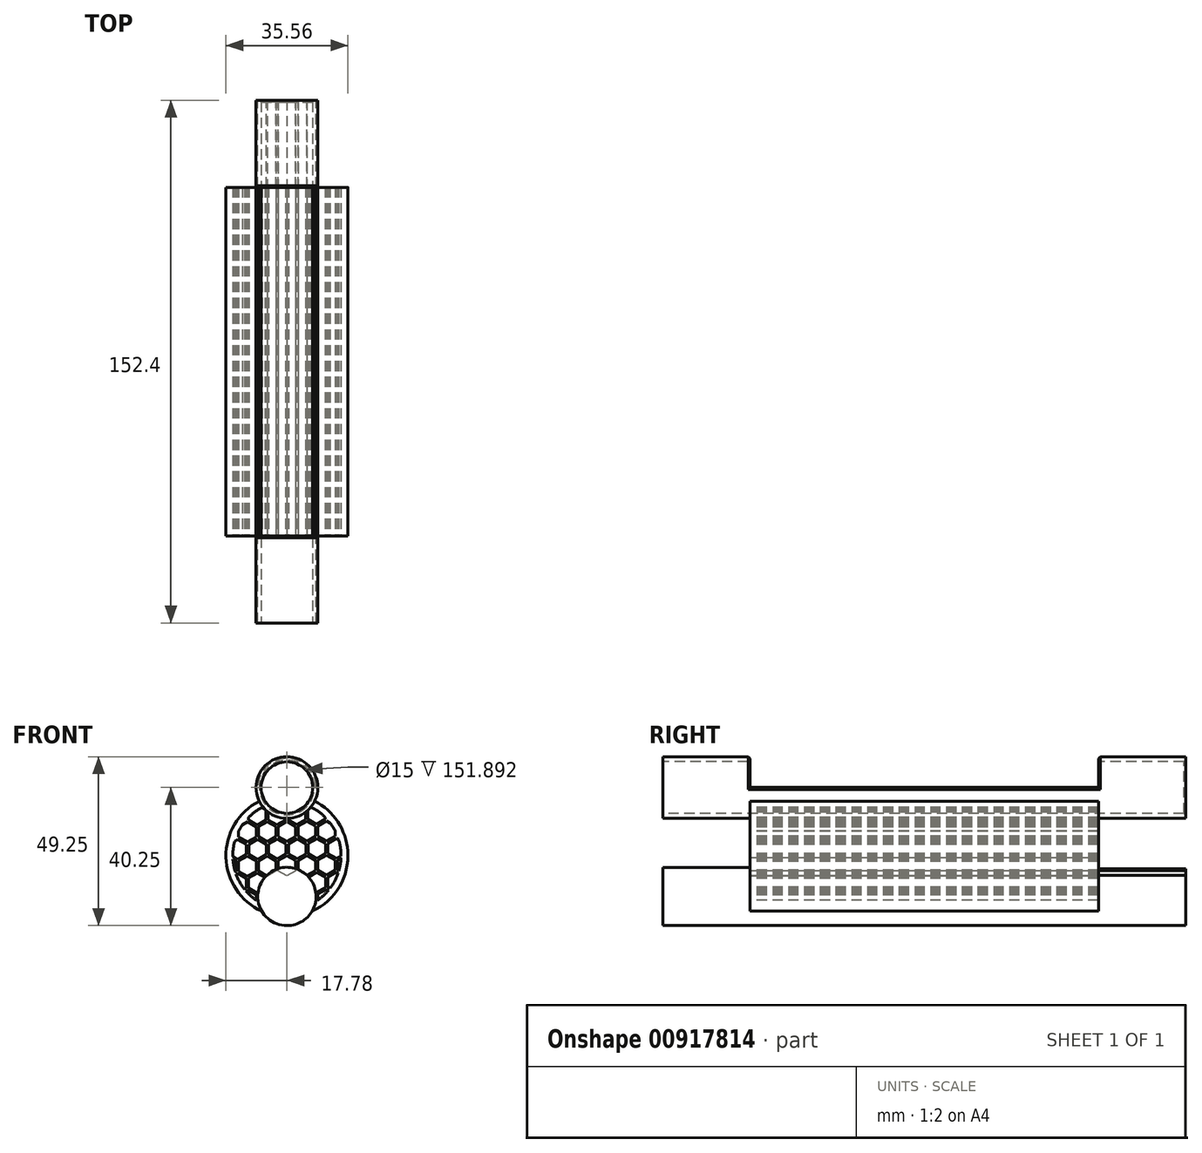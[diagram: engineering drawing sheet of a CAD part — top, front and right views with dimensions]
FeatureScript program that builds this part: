
annotation { "Feature Type Name" : "Feature", "Feature Type Description" : "" }
export const myFeature = defineFeature(function(context is Context, id is Id, definition is map)
    precondition{}
    {
        {
            var Q0;
            Q0=qCreatedBy(makeId("Front.planeOp"),FACE);
            var sketch = newSketch(context, id + "F0", { "sketchPlane" : qUnion([Q0])});
            skCircle(sketch, "E0", {"center": v(0, 0) * mm, "radius": 9 * mm});
            skCircle(sketch, "E1", {"center": v(0, -31.75) * mm, "radius": 8.5 * mm});
            skSolve(sketch);
        }
        {
            var Q0;
            Q0=qSketchRegion(id+"FUGsYxlSOq7sT89_0",true);
            var Q1;
            Q1=makeQuery(id+"F0.imprint","IMPRINT",FACE,{"disambiguationData":[TD([[makeQuery(id+"F0.imprint","IMPRINT",EDGE,{"derivedFrom":sQuery(id+"F0.wireOp",EDGE,"E0")}),1.0]])]});
            var Q2;
            Q2=makeQuery(id+"F0.imprint","IMPRINT",FACE,{"disambiguationData":[TD([[makeQuery(id+"F0.imprint","IMPRINT",EDGE,{"derivedFrom":sQuery(id+"F0.wireOp",EDGE,"E1")}),1.0]])]});
            extrude(context, id + "F1", {"entities" : qUnion([Q0, Q1, Q2]), "endBound" : BoundingType.SYMMETRIC, "depth" : 152.4 * mm, "offsetDistance" : 25.4 * mm});
        }
        {
            var Q0;
            Q0=makeQuery(id+"F1.opExtrude","CAP_FACE",FACE,{"disambiguationData":[OSD([sQuery(id+"F0.wireOp",EDGE,"E0")])],"isStart":false});
            var sketch = newSketch(context, id + "F2", { "sketchPlane" : qUnion([Q0])});
            skCircle(sketch, "E2", {"center": v(0, 0) * mm, "radius": 7.5 * mm});
            skSolve(sketch);
        }
        {
            var Q0;
            Q0=qSketchRegion(id+"F2",true);
            extrude(context, id + "F3", {"entities" : qUnion([Q0]), "operationType" : NewBodyOperationType.REMOVE, "endBound" : BoundingType.THROUGH_ALL, "oppositeDirection" : true, "depth" : 25.4 * mm, "offsetDistance" : 25.4 * mm});
        }
        {
            var Q0;
            Q0=makeQuery(id+"F0.imprint","IMPRINT",FACE,{"disambiguationData":[TD([[makeQuery(id+"F0.imprint","IMPRINT",EDGE,{"derivedFrom":sQuery(id+"F0.wireOp",EDGE,"E0")}),1.0]])]});
            var sketch = newSketch(context, id + "F4", { "sketchPlane" : qUnion([Q0])});
            skLineSegment(sketch, "E3.bottom", {"start": v(-11.18, 12.2) * mm, "end": v(12.33, 12.2) * mm});
            skLineSegment(sketch, "E3.top", {"start": v(-11.18, 0) * mm, "end": v(12.33, 0) * mm});
            skLineSegment(sketch, "E3.left", {"start": v(-11.18, 12.2) * mm, "end": v(-11.18, 0) * mm});
            skLineSegment(sketch, "E3.right", {"start": v(12.33, 12.2) * mm, "end": v(12.33, 0) * mm});
            skSolve(sketch);
        }
        {
            var Q0;
            Q0=qSketchRegion(id+"F4",true);
            extrude(context, id + "F5", {"entities" : qUnion([Q0]), "operationType" : NewBodyOperationType.REMOVE, "endBound" : BoundingType.SYMMETRIC, "oppositeDirection" : true, "depth" : 101.6 * mm, "offsetDistance" : 25.4 * mm});
        }
        {
            var Q0;
            Q0=makeQuery(id+"F5.boolean.opBoolean","INTERSECT",EDGE,{"disambiguationData":[OD(0.0)],"derivedFrom":[makeQuery(id+"F1.opExtrude","SWEPT_FACE",FACE,{"disambiguationData":[OSD([sQuery(id+"F0.wireOp",EDGE,"E0")])]}),makeQuery(id+"F5.opExtrude","SWEPT_FACE",FACE,{"disambiguationData":[OSD([sQuery(id+"F4.wireOp",EDGE,"E3.top")])]})]});
            var Q1;
            Q1=makeQuery(id+"F5.boolean.opBoolean","INTERSECT",EDGE,{"disambiguationData":[OD(1.0)],"derivedFrom":[makeQuery(id+"F1.opExtrude","SWEPT_FACE",FACE,{"disambiguationData":[OSD([sQuery(id+"F0.wireOp",EDGE,"E0")])]}),makeQuery(id+"F5.opExtrude","SWEPT_FACE",FACE,{"disambiguationData":[OSD([sQuery(id+"F4.wireOp",EDGE,"E3.top")])]})]});
            var Q2;
            Q2=makeQuery(id+"F5.boolean.opBoolean","INTERSECT",EDGE,{"disambiguationData":[OD(1.0)],"derivedFrom":[makeQuery(id+"F3.boolean.opBoolean","COPY",FACE,{"derivedFrom":makeQuery(id+"F3.opExtrude","SWEPT_FACE",FACE,{"disambiguationData":[OSD([sQuery(id+"F2.wireOp",EDGE,"E2")])]})}),makeQuery(id+"F5.opExtrude","SWEPT_FACE",FACE,{"disambiguationData":[OSD([sQuery(id+"F4.wireOp",EDGE,"E3.top")])]})]});
            var Q3;
            Q3=makeQuery(id+"F5.boolean.opBoolean","INTERSECT",EDGE,{"disambiguationData":[OD(0.0)],"derivedFrom":[makeQuery(id+"F3.boolean.opBoolean","COPY",FACE,{"derivedFrom":makeQuery(id+"F3.opExtrude","SWEPT_FACE",FACE,{"disambiguationData":[OSD([sQuery(id+"F2.wireOp",EDGE,"E2")])]})}),makeQuery(id+"F5.opExtrude","SWEPT_FACE",FACE,{"disambiguationData":[OSD([sQuery(id+"F4.wireOp",EDGE,"E3.top")])]})]});
            var Q4;
            Q4=makeQuery(id+"F5.boolean.opBoolean","INTERSECT",EDGE,{"derivedFrom":[makeQuery(id+"F1.opExtrude","SWEPT_FACE",FACE,{"disambiguationData":[OSD([sQuery(id+"F0.wireOp",EDGE,"E0")])]}),makeQuery(id+"F5.opExtrude","CAP_FACE",FACE,{"disambiguationData":[OSD([sQuery(id+"F4.wireOp",EDGE,"E3.bottom"),sQuery(id+"F4.wireOp",EDGE,"E3.top"),sQuery(id+"F4.wireOp",EDGE,"E3.left"),sQuery(id+"F4.wireOp",EDGE,"E3.right")])],"isStart":true})]});
            var Q5;
            Q5=makeQuery(id+"F5.boolean.opBoolean","INTERSECT",EDGE,{"derivedFrom":[makeQuery(id+"F1.opExtrude","SWEPT_FACE",FACE,{"disambiguationData":[OSD([sQuery(id+"F0.wireOp",EDGE,"E0")])]}),makeQuery(id+"F5.opExtrude","CAP_FACE",FACE,{"disambiguationData":[OSD([sQuery(id+"F4.wireOp",EDGE,"E3.bottom"),sQuery(id+"F4.wireOp",EDGE,"E3.top"),sQuery(id+"F4.wireOp",EDGE,"E3.left"),sQuery(id+"F4.wireOp",EDGE,"E3.right")])],"isStart":false})]});
            var Q6;
            Q6=makeQuery(id+"F5.boolean.opBoolean","INTERSECT",EDGE,{"derivedFrom":[makeQuery(id+"F3.boolean.opBoolean","COPY",FACE,{"derivedFrom":makeQuery(id+"F3.opExtrude","SWEPT_FACE",FACE,{"disambiguationData":[OSD([sQuery(id+"F2.wireOp",EDGE,"E2")])]})}),makeQuery(id+"F5.opExtrude","CAP_FACE",FACE,{"disambiguationData":[OSD([sQuery(id+"F4.wireOp",EDGE,"E3.bottom"),sQuery(id+"F4.wireOp",EDGE,"E3.top"),sQuery(id+"F4.wireOp",EDGE,"E3.left"),sQuery(id+"F4.wireOp",EDGE,"E3.right")])],"isStart":false})]});
            var Q7;
            Q7=makeQuery(id+"F5.boolean.opBoolean","INTERSECT",EDGE,{"derivedFrom":[makeQuery(id+"F3.boolean.opBoolean","COPY",FACE,{"derivedFrom":makeQuery(id+"F3.opExtrude","SWEPT_FACE",FACE,{"disambiguationData":[OSD([sQuery(id+"F2.wireOp",EDGE,"E2")])]})}),makeQuery(id+"F5.opExtrude","CAP_FACE",FACE,{"disambiguationData":[OSD([sQuery(id+"F4.wireOp",EDGE,"E3.bottom"),sQuery(id+"F4.wireOp",EDGE,"E3.top"),sQuery(id+"F4.wireOp",EDGE,"E3.left"),sQuery(id+"F4.wireOp",EDGE,"E3.right")])],"isStart":true})]});
            var Q8;
            Q8=makeQuery(id+"F3.boolean.opBoolean","INTERSECT",EDGE,{"derivedFrom":[makeQuery(id+"F1.opExtrude","CAP_FACE",FACE,{"disambiguationData":[OSD([sQuery(id+"F0.wireOp",EDGE,"E0")])],"isStart":true}),makeQuery(id+"F3.opExtrude","SWEPT_FACE",FACE,{"disambiguationData":[OSD([sQuery(id+"F2.wireOp",EDGE,"E2")])]})]});
            var Q9;
            Q9=makeQuery(id+"F3.boolean.opBoolean","COPY",EDGE,{"derivedFrom":makeQuery(id+"F3.opExtrude","CAP_EDGE",EDGE,{"disambiguationData":[OSD([sQuery(id+"F2.wireOp",EDGE,"E2")])],"isStart":true})});
            chamfer(context, id + "F6", {"entities" : qUnion([Q0, Q1, Q2, Q3, Q4, Q5, Q6, Q7, Q8, Q9]), "width" : 0.5 * mm, "tangentPropagation" : true});
        }
        {
            var Q0;
            Q0=qCreatedBy(makeId("Front.planeOp"),FACE);
            var sketch = newSketch(context, id + "F7", { "sketchPlane" : qUnion([Q0])});
            skLineSegment(sketch, "E4.0", {"start": v(2, -31.75) * mm, "end": v(2, -8.64) * mm});
            skLineSegment(sketch, "E5.0", {"start": v(-2, -31.75) * mm, "end": v(-2, -8.64) * mm});
            skPoint(sketch, "E6.start.orphan", {"position": v(0, -31.75) * mm});
            skLineSegment(sketch, "E7", {"start": v(-2, -31.75) * mm, "end": v(2, -31.75) * mm});
            skLineSegment(sketch, "E8", {"start": v(2, -8.64) * mm, "end": v(-2, -8.64) * mm});
            skSolve(sketch);
        }
        {
            var Q0;
            Q0=qSketchRegion(id+"F7",true);
            extrude(context, id + "F8", {"entities" : qUnion([Q0]), "operationType" : NewBodyOperationType.ADD, "endBound" : BoundingType.SYMMETRIC, "oppositeDirection" : true, "depth" : 101.6 * mm, "offsetDistance" : 25.4 * mm});
        }
        {
            var Q0;
            Q0=qCreatedBy(makeId("Front.planeOp"),FACE);
            var sketch = newSketch(context, id + "F9", { "sketchPlane" : qUnion([Q0])});
            skCircle(sketch, "E9", {"center": v(0, -19.81) * mm, "radius": 17.78 * mm});
            skSolve(sketch);
        }
        {
            var Q0;
            Q0=qSketchRegion(id+"F9",true);
            extrude(context, id + "F10", {"entities" : qUnion([Q0]), "operationType" : NewBodyOperationType.ADD, "endBound" : BoundingType.SYMMETRIC, "depth" : 101.6 * mm, "offsetDistance" : 25.4 * mm});
        }
        {
            var Q0;
            Q0=makeQuery(id+"F0.imprint","IMPRINT",FACE,{"disambiguationData":[TD([[makeQuery(id+"F0.imprint","IMPRINT",EDGE,{"derivedFrom":sQuery(id+"F0.wireOp",EDGE,"E0")}),1.0]])]});
            var sketch = newSketch(context, id + "F11", { "sketchPlane" : qUnion([Q0])});
            skCircle(sketch, "E10", {"center": v(0, 0) * mm, "radius": 7.5 * mm});
            skSolve(sketch);
        }
        {
            var Q0;
            Q0=qSketchRegion(id+"F11",true);
            extrude(context, id + "F12", {"entities" : qUnion([Q0]), "operationType" : NewBodyOperationType.REMOVE, "endBound" : BoundingType.SYMMETRIC, "oppositeDirection" : true, "depth" : 152.4 * mm, "offsetDistance" : 25.4 * mm});
        }
        {
            var Q0;
            Q0=makeQuery(id+"F10.boolean.opBoolean","MERGE",FACE,{"derivedFrom":[makeQuery(id+"F8.opExtrude","CAP_FACE",FACE,{"disambiguationData":[OSD([sQuery(id+"F7.wireOp",EDGE,"E4.0"),sQuery(id+"F7.wireOp",EDGE,"E5.0"),sQuery(id+"F7.wireOp",EDGE,"E7"),sQuery(id+"F7.wireOp",EDGE,"E8")])],"isStart":true}),makeQuery(id+"F10.opExtrude","CAP_FACE",FACE,{"disambiguationData":[OSD([sQuery(id+"F9.wireOp",EDGE,"E9")])],"isStart":false})]});
            var sketch = newSketch(context, id + "F13", { "sketchPlane" : qUnion([Q0])});
            skCircle(sketch, "E11.cCircle", {"center": v(-11.52, -12.94) * mm, "radius": 2.55 * mm, "construction": true});
            skLineSegment(sketch, "E11.0", {"start": v(-8.97, -11.46) * mm, "end": v(-8.97, -14.4) * mm});
            skLineSegment(sketch, "E11.1", {"start": v(-8.97, -14.4) * mm, "end": v(-11.52, -15.88) * mm});
            skLineSegment(sketch, "E11.2", {"start": v(-11.52, -15.88) * mm, "end": v(-14.07, -14.4) * mm});
            skLineSegment(sketch, "E11.3", {"start": v(-14.07, -14.4) * mm, "end": v(-14.07, -11.46) * mm});
            skLineSegment(sketch, "E11.4", {"start": v(-14.07, -11.46) * mm, "end": v(-11.52, -10) * mm});
            skLineSegment(sketch, "E11.5", {"start": v(-11.52, -10) * mm, "end": v(-8.97, -11.46) * mm});
            skPoint(sketch, "E11.0.midPoint", {"position": v(-8.97, -12.94) * mm});
            skLineSegment(sketch, "E12.1.0.0", {"start": v(-5.75, -9.92) * mm, "end": v(-3.2, -11.4) * mm});
            skLineSegment(sketch, "E12.1.0.1", {"start": v(-8.3, -11.4) * mm, "end": v(-5.75, -9.92) * mm});
            skLineSegment(sketch, "E12.1.0.2", {"start": v(-8.3, -14.34) * mm, "end": v(-8.3, -11.4) * mm});
            skLineSegment(sketch, "E12.1.0.3", {"start": v(-5.75, -15.81) * mm, "end": v(-8.3, -14.34) * mm});
            skLineSegment(sketch, "E12.1.0.4", {"start": v(-3.2, -11.4) * mm, "end": v(-3.2, -14.34) * mm});
            skLineSegment(sketch, "E12.1.0.5", {"start": v(-3.2, -14.34) * mm, "end": v(-5.75, -15.81) * mm});
            skLineSegment(sketch, "E12.2.0.0", {"start": v(0.02, -9.85) * mm, "end": v(2.57, -11.33) * mm});
            skLineSegment(sketch, "E12.2.0.1", {"start": v(-2.53, -11.33) * mm, "end": v(0.02, -9.85) * mm});
            skLineSegment(sketch, "E12.2.0.2", {"start": v(-2.53, -14.27) * mm, "end": v(-2.53, -11.33) * mm});
            skLineSegment(sketch, "E12.2.0.3", {"start": v(0.02, -15.74) * mm, "end": v(-2.53, -14.27) * mm});
            skLineSegment(sketch, "E12.2.0.4", {"start": v(2.57, -11.33) * mm, "end": v(2.57, -14.27) * mm});
            skLineSegment(sketch, "E12.2.0.5", {"start": v(2.57, -14.27) * mm, "end": v(0.02, -15.74) * mm});
            skLineSegment(sketch, "E12.3.0.0", {"start": v(5.78, -9.79) * mm, "end": v(8.33, -11.26) * mm});
            skLineSegment(sketch, "E12.3.0.1", {"start": v(3.23, -11.26) * mm, "end": v(5.78, -9.79) * mm});
            skLineSegment(sketch, "E12.3.0.2", {"start": v(3.23, -14.2) * mm, "end": v(3.23, -11.26) * mm});
            skLineSegment(sketch, "E12.3.0.3", {"start": v(5.78, -15.67) * mm, "end": v(3.23, -14.2) * mm});
            skLineSegment(sketch, "E12.3.0.4", {"start": v(8.33, -11.26) * mm, "end": v(8.33, -14.2) * mm});
            skLineSegment(sketch, "E12.3.0.5", {"start": v(8.33, -14.2) * mm, "end": v(5.78, -15.67) * mm});
            skLineSegment(sketch, "E12.4.0.0", {"start": v(11.55, -9.72) * mm, "end": v(14.1, -11.19) * mm});
            skLineSegment(sketch, "E12.4.0.1", {"start": v(9, -11.19) * mm, "end": v(11.55, -9.72) * mm});
            skLineSegment(sketch, "E12.4.0.2", {"start": v(9, -14.13) * mm, "end": v(9, -11.19) * mm});
            skLineSegment(sketch, "E12.4.0.3", {"start": v(11.55, -15.6) * mm, "end": v(9, -14.13) * mm});
            skLineSegment(sketch, "E12.4.0.4", {"start": v(14.1, -11.19) * mm, "end": v(14.1, -14.13) * mm});
            skLineSegment(sketch, "E12.4.0.5", {"start": v(14.1, -14.13) * mm, "end": v(11.55, -15.6) * mm});
            skLineSegment(sketch, "E12.direction1", {"start": v(-11.52, -10) * mm, "end": v(-5.75, -9.92) * mm, "construction": true});
            skSolve(sketch);
        }
        {
            var Q0;
            Q0=qSketchRegion(id+"F13",true);
            extrude(context, id + "F14", {"entities" : qUnion([Q0]), "operationType" : NewBodyOperationType.REMOVE, "oppositeDirection" : true, "depth" : 177.8 * mm, "offsetDistance" : 25.4 * mm});
        }
        {
            var Q0;
            Q0=makeQuery(id+"F10.boolean.opBoolean","MERGE",FACE,{"derivedFrom":[makeQuery(id+"F8.opExtrude","CAP_FACE",FACE,{"disambiguationData":[OSD([sQuery(id+"F7.wireOp",EDGE,"E4.0"),sQuery(id+"F7.wireOp",EDGE,"E5.0"),sQuery(id+"F7.wireOp",EDGE,"E7"),sQuery(id+"F7.wireOp",EDGE,"E8")])],"isStart":true}),makeQuery(id+"F10.opExtrude","CAP_FACE",FACE,{"disambiguationData":[OSD([sQuery(id+"F9.wireOp",EDGE,"E9")])],"isStart":false})]});
            var sketch = newSketch(context, id + "F15", { "sketchPlane" : qUnion([Q0])});
            skCircle(sketch, "E13.cCircle", {"center": v(-14.33, -18.09) * mm, "radius": 2.55 * mm, "construction": true});
            skLineSegment(sketch, "E13.0", {"start": v(-11.78, -16.61) * mm, "end": v(-11.78, -19.56) * mm});
            skLineSegment(sketch, "E13.1", {"start": v(-11.78, -19.56) * mm, "end": v(-14.33, -21.03) * mm});
            skLineSegment(sketch, "E13.2", {"start": v(-14.33, -21.03) * mm, "end": v(-16.88, -19.56) * mm});
            skLineSegment(sketch, "E13.3", {"start": v(-16.88, -19.56) * mm, "end": v(-16.88, -16.61) * mm});
            skLineSegment(sketch, "E13.4", {"start": v(-16.88, -16.61) * mm, "end": v(-14.33, -15.14) * mm});
            skLineSegment(sketch, "E13.5", {"start": v(-14.33, -15.14) * mm, "end": v(-11.78, -16.61) * mm});
            skPoint(sketch, "E13.0.midPoint", {"position": v(-11.78, -18.09) * mm});
            skLineSegment(sketch, "E14.1.0.0", {"start": v(-8.56, -15.07) * mm, "end": v(-6.01, -16.55) * mm});
            skLineSegment(sketch, "E14.1.0.1", {"start": v(-11.11, -16.55) * mm, "end": v(-8.56, -15.07) * mm});
            skLineSegment(sketch, "E14.1.0.2", {"start": v(-11.11, -19.5) * mm, "end": v(-11.11, -16.55) * mm});
            skLineSegment(sketch, "E14.1.0.3", {"start": v(-8.56, -20.96) * mm, "end": v(-11.11, -19.5) * mm});
            skLineSegment(sketch, "E14.1.0.4", {"start": v(-6.01, -16.55) * mm, "end": v(-6.01, -19.5) * mm});
            skLineSegment(sketch, "E14.1.0.5", {"start": v(-6.01, -19.5) * mm, "end": v(-8.56, -20.96) * mm});
            skLineSegment(sketch, "E14.2.0.0", {"start": v(-2.8, -15) * mm, "end": v(-0.25, -16.48) * mm});
            skLineSegment(sketch, "E14.2.0.1", {"start": v(-5.35, -16.48) * mm, "end": v(-2.8, -15) * mm});
            skLineSegment(sketch, "E14.2.0.2", {"start": v(-5.35, -19.42) * mm, "end": v(-5.35, -16.48) * mm});
            skLineSegment(sketch, "E14.2.0.3", {"start": v(-2.8, -20.9) * mm, "end": v(-5.35, -19.42) * mm});
            skLineSegment(sketch, "E14.2.0.4", {"start": v(-0.25, -16.48) * mm, "end": v(-0.25, -19.42) * mm});
            skLineSegment(sketch, "E14.2.0.5", {"start": v(-0.25, -19.42) * mm, "end": v(-2.8, -20.9) * mm});
            skLineSegment(sketch, "E14.3.0.0", {"start": v(2.97, -14.94) * mm, "end": v(5.52, -16.4) * mm});
            skLineSegment(sketch, "E14.3.0.1", {"start": v(0.42, -16.4) * mm, "end": v(2.97, -14.94) * mm});
            skLineSegment(sketch, "E14.3.0.2", {"start": v(0.42, -19.35) * mm, "end": v(0.42, -16.4) * mm});
            skLineSegment(sketch, "E14.3.0.3", {"start": v(2.97, -20.83) * mm, "end": v(0.42, -19.35) * mm});
            skLineSegment(sketch, "E14.3.0.4", {"start": v(5.52, -16.4) * mm, "end": v(5.52, -19.35) * mm});
            skLineSegment(sketch, "E14.3.0.5", {"start": v(5.52, -19.35) * mm, "end": v(2.97, -20.83) * mm});
            skLineSegment(sketch, "E14.4.0.0", {"start": v(8.73, -14.87) * mm, "end": v(11.28, -16.34) * mm});
            skLineSegment(sketch, "E14.4.0.1", {"start": v(6.18, -16.34) * mm, "end": v(8.73, -14.87) * mm});
            skLineSegment(sketch, "E14.4.0.2", {"start": v(6.18, -19.28) * mm, "end": v(6.18, -16.34) * mm});
            skLineSegment(sketch, "E14.4.0.3", {"start": v(8.73, -20.76) * mm, "end": v(6.18, -19.28) * mm});
            skLineSegment(sketch, "E14.4.0.4", {"start": v(11.28, -16.34) * mm, "end": v(11.28, -19.28) * mm});
            skLineSegment(sketch, "E14.4.0.5", {"start": v(11.28, -19.28) * mm, "end": v(8.73, -20.76) * mm});
            skLineSegment(sketch, "E14.direction1", {"start": v(-14.33, -15.14) * mm, "end": v(-8.56, -15.07) * mm, "construction": true});
            skLineSegment(sketch, "E15.0.5.0", {"start": v(14.5, -14.8) * mm, "end": v(17.05, -16.27) * mm});
            skLineSegment(sketch, "E15.3.5.0", {"start": v(11.95, -16.27) * mm, "end": v(14.5, -14.8) * mm});
            skLineSegment(sketch, "E15.6.5.0", {"start": v(11.95, -19.22) * mm, "end": v(11.95, -16.27) * mm});
            skLineSegment(sketch, "E15.9.5.0", {"start": v(14.5, -20.69) * mm, "end": v(11.95, -19.22) * mm});
            skLineSegment(sketch, "E15.12.5.0", {"start": v(17.05, -16.27) * mm, "end": v(17.05, -19.22) * mm});
            skLineSegment(sketch, "E15.15.5.0", {"start": v(17.05, -19.22) * mm, "end": v(14.5, -20.69) * mm});
            skSolve(sketch);
        }
        {
            var Q0;
            Q0=qSketchRegion(id+"F15",true);
            extrude(context, id + "F16", {"entities" : qUnion([Q0]), "operationType" : NewBodyOperationType.REMOVE, "oppositeDirection" : true, "depth" : 177.8 * mm, "offsetDistance" : 25.4 * mm});
        }
        {
            var Q0;
            Q0=makeQuery(id+"F10.boolean.opBoolean","MERGE",FACE,{"derivedFrom":[makeQuery(id+"F8.opExtrude","CAP_FACE",FACE,{"disambiguationData":[OSD([sQuery(id+"F7.wireOp",EDGE,"E4.0"),sQuery(id+"F7.wireOp",EDGE,"E5.0"),sQuery(id+"F7.wireOp",EDGE,"E7"),sQuery(id+"F7.wireOp",EDGE,"E8")])],"isStart":true}),makeQuery(id+"F10.opExtrude","CAP_FACE",FACE,{"disambiguationData":[OSD([sQuery(id+"F9.wireOp",EDGE,"E9")])],"isStart":false})]});
            var sketch = newSketch(context, id + "F17", { "sketchPlane" : qUnion([Q0])});
            skCircle(sketch, "E16.cCircle", {"center": v(-17.3, -23) * mm, "radius": 2.55 * mm, "construction": true});
            skLineSegment(sketch, "E16.0", {"start": v(-14.75, -21.52) * mm, "end": v(-14.75, -24.47) * mm});
            skLineSegment(sketch, "E16.1", {"start": v(-14.75, -24.47) * mm, "end": v(-17.3, -25.94) * mm});
            skLineSegment(sketch, "E16.2", {"start": v(-17.3, -25.94) * mm, "end": v(-19.84, -24.47) * mm});
            skLineSegment(sketch, "E16.3", {"start": v(-19.84, -24.47) * mm, "end": v(-19.84, -21.52) * mm});
            skLineSegment(sketch, "E16.4", {"start": v(-19.84, -21.52) * mm, "end": v(-17.3, -20.05) * mm});
            skLineSegment(sketch, "E16.5", {"start": v(-17.3, -20.05) * mm, "end": v(-14.75, -21.52) * mm});
            skPoint(sketch, "E16.0.midPoint", {"position": v(-14.75, -23) * mm});
            skLineSegment(sketch, "E17.1.0.0", {"start": v(-11.53, -19.98) * mm, "end": v(-8.98, -21.46) * mm});
            skLineSegment(sketch, "E17.1.0.1", {"start": v(-14.08, -21.46) * mm, "end": v(-11.53, -19.98) * mm});
            skLineSegment(sketch, "E17.1.0.2", {"start": v(-14.08, -24.4) * mm, "end": v(-14.08, -21.46) * mm});
            skLineSegment(sketch, "E17.1.0.3", {"start": v(-11.53, -25.87) * mm, "end": v(-14.08, -24.4) * mm});
            skLineSegment(sketch, "E17.1.0.4", {"start": v(-8.98, -21.46) * mm, "end": v(-8.98, -24.4) * mm});
            skLineSegment(sketch, "E17.1.0.5", {"start": v(-8.98, -24.4) * mm, "end": v(-11.53, -25.87) * mm});
            skLineSegment(sketch, "E17.direction1", {"start": v(-17.3, -20.05) * mm, "end": v(-11.53, -19.98) * mm, "construction": true});
            skLineSegment(sketch, "E18.0.2.0", {"start": v(-5.76, -19.91) * mm, "end": v(-3.21, -21.39) * mm});
            skLineSegment(sketch, "E18.3.2.0", {"start": v(-8.31, -21.39) * mm, "end": v(-5.76, -19.91) * mm});
            skLineSegment(sketch, "E18.6.2.0", {"start": v(-8.31, -24.33) * mm, "end": v(-8.31, -21.39) * mm});
            skLineSegment(sketch, "E18.9.2.0", {"start": v(-5.76, -25.8) * mm, "end": v(-8.31, -24.33) * mm});
            skLineSegment(sketch, "E18.12.2.0", {"start": v(-3.21, -21.39) * mm, "end": v(-3.21, -24.33) * mm});
            skLineSegment(sketch, "E18.15.2.0", {"start": v(-3.21, -24.33) * mm, "end": v(-5.76, -25.8) * mm});
            skLineSegment(sketch, "E18.0.3.0", {"start": v(0, -19.85) * mm, "end": v(2.55, -21.32) * mm});
            skLineSegment(sketch, "E18.3.3.0", {"start": v(-2.55, -21.32) * mm, "end": v(0, -19.85) * mm});
            skLineSegment(sketch, "E18.6.3.0", {"start": v(-2.55, -24.26) * mm, "end": v(-2.55, -21.32) * mm});
            skLineSegment(sketch, "E18.9.3.0", {"start": v(0, -25.74) * mm, "end": v(-2.55, -24.26) * mm});
            skLineSegment(sketch, "E18.12.3.0", {"start": v(2.55, -21.32) * mm, "end": v(2.55, -24.26) * mm});
            skLineSegment(sketch, "E18.15.3.0", {"start": v(2.55, -24.26) * mm, "end": v(0, -25.74) * mm});
            skLineSegment(sketch, "E18.0.4.0", {"start": v(5.77, -19.78) * mm, "end": v(8.32, -21.25) * mm});
            skLineSegment(sketch, "E18.3.4.0", {"start": v(3.22, -21.25) * mm, "end": v(5.77, -19.78) * mm});
            skLineSegment(sketch, "E18.6.4.0", {"start": v(3.22, -24.2) * mm, "end": v(3.22, -21.25) * mm});
            skLineSegment(sketch, "E18.9.4.0", {"start": v(5.77, -25.67) * mm, "end": v(3.22, -24.2) * mm});
            skLineSegment(sketch, "E18.12.4.0", {"start": v(8.32, -21.25) * mm, "end": v(8.32, -24.2) * mm});
            skLineSegment(sketch, "E18.15.4.0", {"start": v(8.32, -24.2) * mm, "end": v(5.77, -25.67) * mm});
            skLineSegment(sketch, "E19.0.5.0", {"start": v(11.53, -19.7) * mm, "end": v(14.08, -21.18) * mm});
            skLineSegment(sketch, "E19.3.5.0", {"start": v(8.98, -21.18) * mm, "end": v(11.53, -19.7) * mm});
            skLineSegment(sketch, "E19.6.5.0", {"start": v(8.98, -24.13) * mm, "end": v(8.98, -21.18) * mm});
            skLineSegment(sketch, "E19.9.5.0", {"start": v(11.53, -25.6) * mm, "end": v(8.98, -24.13) * mm});
            skLineSegment(sketch, "E19.12.5.0", {"start": v(14.08, -21.18) * mm, "end": v(14.08, -24.13) * mm});
            skLineSegment(sketch, "E19.15.5.0", {"start": v(14.08, -24.13) * mm, "end": v(11.53, -25.6) * mm});
            skLineSegment(sketch, "E20.0.6.0", {"start": v(17.3, -19.64) * mm, "end": v(19.85, -21.11) * mm});
            skLineSegment(sketch, "E20.3.6.0", {"start": v(14.75, -21.11) * mm, "end": v(17.3, -19.64) * mm});
            skLineSegment(sketch, "E20.6.6.0", {"start": v(14.75, -24.06) * mm, "end": v(14.75, -21.11) * mm});
            skLineSegment(sketch, "E20.9.6.0", {"start": v(17.3, -25.53) * mm, "end": v(14.75, -24.06) * mm});
            skLineSegment(sketch, "E20.12.6.0", {"start": v(19.85, -21.11) * mm, "end": v(19.85, -24.06) * mm});
            skLineSegment(sketch, "E20.15.6.0", {"start": v(19.85, -24.06) * mm, "end": v(17.3, -25.53) * mm});
            skSolve(sketch);
        }
        {
            var Q0;
            Q0=qSketchRegion(id+"F17",true);
            extrude(context, id + "F18", {"entities" : qUnion([Q0]), "operationType" : NewBodyOperationType.REMOVE, "endBound" : BoundingType.THROUGH_ALL, "oppositeDirection" : true, "depth" : 25.4 * mm, "offsetDistance" : 25.4 * mm});
        }
        {
            var Q0;
            Q0=makeQuery(id+"F10.boolean.opBoolean","MERGE",FACE,{"derivedFrom":[makeQuery(id+"F8.opExtrude","CAP_FACE",FACE,{"disambiguationData":[OSD([sQuery(id+"F7.wireOp",EDGE,"E4.0"),sQuery(id+"F7.wireOp",EDGE,"E5.0"),sQuery(id+"F7.wireOp",EDGE,"E7"),sQuery(id+"F7.wireOp",EDGE,"E8")])],"isStart":true}),makeQuery(id+"F10.opExtrude","CAP_FACE",FACE,{"disambiguationData":[OSD([sQuery(id+"F9.wireOp",EDGE,"E9")])],"isStart":false})]});
            var sketch = newSketch(context, id + "F19", { "sketchPlane" : qUnion([Q0])});
            skCircle(sketch, "E21.cCircle", {"center": v(-14.4, -27.92) * mm, "radius": 2.55 * mm, "construction": true});
            skLineSegment(sketch, "E21.0", {"start": v(-11.84, -26.45) * mm, "end": v(-11.84, -29.4) * mm});
            skLineSegment(sketch, "E21.1", {"start": v(-11.84, -29.4) * mm, "end": v(-14.4, -30.86) * mm});
            skLineSegment(sketch, "E21.2", {"start": v(-14.4, -30.86) * mm, "end": v(-16.94, -29.4) * mm});
            skLineSegment(sketch, "E21.3", {"start": v(-16.94, -29.4) * mm, "end": v(-16.94, -26.45) * mm});
            skLineSegment(sketch, "E21.4", {"start": v(-16.94, -26.45) * mm, "end": v(-14.4, -24.98) * mm});
            skLineSegment(sketch, "E21.5", {"start": v(-14.4, -24.98) * mm, "end": v(-11.84, -26.45) * mm});
            skPoint(sketch, "E21.0.midPoint", {"position": v(-11.84, -27.92) * mm});
            skLineSegment(sketch, "E22.1.0.0", {"start": v(-8.63, -24.9) * mm, "end": v(-6.08, -26.38) * mm});
            skLineSegment(sketch, "E22.1.0.1", {"start": v(-11.18, -26.38) * mm, "end": v(-8.63, -24.9) * mm});
            skLineSegment(sketch, "E22.1.0.2", {"start": v(-11.18, -29.32) * mm, "end": v(-11.18, -26.38) * mm});
            skLineSegment(sketch, "E22.1.0.3", {"start": v(-8.63, -30.8) * mm, "end": v(-11.18, -29.32) * mm});
            skLineSegment(sketch, "E22.1.0.4", {"start": v(-6.08, -26.38) * mm, "end": v(-6.08, -29.32) * mm});
            skLineSegment(sketch, "E22.1.0.5", {"start": v(-6.08, -29.32) * mm, "end": v(-8.63, -30.8) * mm});
            skLineSegment(sketch, "E22.2.0.0", {"start": v(-2.86, -24.84) * mm, "end": v(-0.31, -26.31) * mm});
            skLineSegment(sketch, "E22.2.0.1", {"start": v(-5.41, -26.31) * mm, "end": v(-2.86, -24.84) * mm});
            skLineSegment(sketch, "E22.2.0.2", {"start": v(-5.41, -29.25) * mm, "end": v(-5.41, -26.31) * mm});
            skLineSegment(sketch, "E22.2.0.3", {"start": v(-2.86, -30.73) * mm, "end": v(-5.41, -29.25) * mm});
            skLineSegment(sketch, "E22.2.0.4", {"start": v(-0.31, -26.31) * mm, "end": v(-0.31, -29.25) * mm});
            skLineSegment(sketch, "E22.2.0.5", {"start": v(-0.31, -29.25) * mm, "end": v(-2.86, -30.73) * mm});
            skLineSegment(sketch, "E22.3.0.0", {"start": v(2.9, -24.77) * mm, "end": v(5.45, -26.24) * mm});
            skLineSegment(sketch, "E22.3.0.1", {"start": v(0.35, -26.24) * mm, "end": v(2.9, -24.77) * mm});
            skLineSegment(sketch, "E22.3.0.2", {"start": v(0.35, -29.19) * mm, "end": v(0.35, -26.24) * mm});
            skLineSegment(sketch, "E22.3.0.3", {"start": v(2.9, -30.66) * mm, "end": v(0.35, -29.19) * mm});
            skLineSegment(sketch, "E22.3.0.4", {"start": v(5.45, -26.24) * mm, "end": v(5.45, -29.19) * mm});
            skLineSegment(sketch, "E22.3.0.5", {"start": v(5.45, -29.19) * mm, "end": v(2.9, -30.66) * mm});
            skLineSegment(sketch, "E22.4.0.0", {"start": v(8.67, -24.7) * mm, "end": v(11.22, -26.17) * mm});
            skLineSegment(sketch, "E22.4.0.1", {"start": v(6.12, -26.17) * mm, "end": v(8.67, -24.7) * mm});
            skLineSegment(sketch, "E22.4.0.2", {"start": v(6.12, -29.12) * mm, "end": v(6.12, -26.17) * mm});
            skLineSegment(sketch, "E22.4.0.3", {"start": v(8.67, -30.6) * mm, "end": v(6.12, -29.12) * mm});
            skLineSegment(sketch, "E22.4.0.4", {"start": v(11.22, -26.17) * mm, "end": v(11.22, -29.12) * mm});
            skLineSegment(sketch, "E22.4.0.5", {"start": v(11.22, -29.12) * mm, "end": v(8.67, -30.6) * mm});
            skLineSegment(sketch, "E22.direction1", {"start": v(-14.4, -24.98) * mm, "end": v(-8.63, -24.9) * mm, "construction": true});
            skLineSegment(sketch, "E23.0.5.0", {"start": v(14.44, -24.63) * mm, "end": v(16.99, -26.1) * mm});
            skLineSegment(sketch, "E23.3.5.0", {"start": v(11.89, -26.1) * mm, "end": v(14.44, -24.63) * mm});
            skLineSegment(sketch, "E23.6.5.0", {"start": v(11.89, -29.05) * mm, "end": v(11.89, -26.1) * mm});
            skLineSegment(sketch, "E23.9.5.0", {"start": v(14.44, -30.52) * mm, "end": v(11.89, -29.05) * mm});
            skLineSegment(sketch, "E23.12.5.0", {"start": v(16.99, -26.1) * mm, "end": v(16.99, -29.05) * mm});
            skLineSegment(sketch, "E23.15.5.0", {"start": v(16.99, -29.05) * mm, "end": v(14.44, -30.52) * mm});
            skSolve(sketch);
        }
        {
            var Q0;
            Q0=makeQuery(id+"F19.imprint","IMPRINT",FACE,{"disambiguationData":[TD([[makeQuery(id+"F19.imprint","IMPRINT",EDGE,{"derivedFrom":sQuery(id+"F19.wireOp",EDGE,"E21.0")}),1.0]])]});
            var sketch = newSketch(context, id + "F20", { "sketchPlane" : qUnion([Q0])});
            skCircle(sketch, "E24.cCircle", {"center": v(-8.71, -8) * mm, "radius": 2.55 * mm, "construction": true});
            skLineSegment(sketch, "E24.0", {"start": v(-6.16, -6.53) * mm, "end": v(-6.16, -9.47) * mm});
            skLineSegment(sketch, "E24.1", {"start": v(-6.16, -9.47) * mm, "end": v(-8.71, -10.94) * mm});
            skLineSegment(sketch, "E24.2", {"start": v(-8.71, -10.94) * mm, "end": v(-11.26, -9.47) * mm});
            skLineSegment(sketch, "E24.3", {"start": v(-11.26, -9.47) * mm, "end": v(-11.26, -6.53) * mm});
            skLineSegment(sketch, "E24.4", {"start": v(-11.26, -6.53) * mm, "end": v(-8.71, -5.06) * mm});
            skLineSegment(sketch, "E24.5", {"start": v(-8.71, -5.06) * mm, "end": v(-6.16, -6.53) * mm});
            skPoint(sketch, "E24.0.midPoint", {"position": v(-6.16, -8) * mm});
            skLineSegment(sketch, "E25.1.0.0", {"start": v(-2.95, -4.99) * mm, "end": v(-0.4, -6.46) * mm});
            skLineSegment(sketch, "E25.1.0.1", {"start": v(-5.5, -6.46) * mm, "end": v(-2.95, -4.99) * mm});
            skLineSegment(sketch, "E25.1.0.2", {"start": v(-5.5, -9.4) * mm, "end": v(-5.5, -6.46) * mm});
            skLineSegment(sketch, "E25.1.0.3", {"start": v(-2.95, -10.88) * mm, "end": v(-5.5, -9.4) * mm});
            skLineSegment(sketch, "E25.1.0.4", {"start": v(-0.4, -6.46) * mm, "end": v(-0.4, -9.4) * mm});
            skLineSegment(sketch, "E25.1.0.5", {"start": v(-0.4, -9.4) * mm, "end": v(-2.95, -10.88) * mm});
            skLineSegment(sketch, "E25.2.0.0", {"start": v(2.82, -4.92) * mm, "end": v(5.37, -6.4) * mm});
            skLineSegment(sketch, "E25.2.0.1", {"start": v(0.27, -6.4) * mm, "end": v(2.82, -4.92) * mm});
            skLineSegment(sketch, "E25.2.0.2", {"start": v(0.27, -9.34) * mm, "end": v(0.27, -6.4) * mm});
            skLineSegment(sketch, "E25.2.0.3", {"start": v(2.82, -10.8) * mm, "end": v(0.27, -9.34) * mm});
            skLineSegment(sketch, "E25.2.0.4", {"start": v(5.37, -6.4) * mm, "end": v(5.37, -9.34) * mm});
            skLineSegment(sketch, "E25.2.0.5", {"start": v(5.37, -9.34) * mm, "end": v(2.82, -10.8) * mm});
            skLineSegment(sketch, "E25.3.0.0", {"start": v(8.59, -4.85) * mm, "end": v(11.14, -6.32) * mm});
            skLineSegment(sketch, "E25.3.0.1", {"start": v(6.04, -6.32) * mm, "end": v(8.59, -4.85) * mm});
            skLineSegment(sketch, "E25.3.0.2", {"start": v(6.04, -9.27) * mm, "end": v(6.04, -6.32) * mm});
            skLineSegment(sketch, "E25.3.0.3", {"start": v(8.59, -10.74) * mm, "end": v(6.04, -9.27) * mm});
            skLineSegment(sketch, "E25.3.0.4", {"start": v(11.14, -6.32) * mm, "end": v(11.14, -9.27) * mm});
            skLineSegment(sketch, "E25.3.0.5", {"start": v(11.14, -9.27) * mm, "end": v(8.59, -10.74) * mm});
            skLineSegment(sketch, "E25.direction1", {"start": v(-8.71, -5.06) * mm, "end": v(-2.95, -4.99) * mm, "construction": true});
            skSolve(sketch);
        }
        {
            var Q0;
            {var subQ30=sQuery(id+"F20.wireOp",EDGE,"E24.1");Q0=makeQuery(id+"F20.imprint","IMPRINT",FACE,{"disambiguationData":[TD([[makeQuery(id+"F20.imprint","IMPRINT",EDGE,{"derivedFrom":subQ30}),1.0]])]});}
            var sketch = newSketch(context, id + "F21", { "sketchPlane" : qUnion([Q0])});
            skCircle(sketch, "E26.cCircle", {"center": v(-11.51, -32.84) * mm, "radius": 2.55 * mm, "construction": true});
            skLineSegment(sketch, "E26.0", {"start": v(-8.96, -31.36) * mm, "end": v(-8.96, -34.3) * mm});
            skLineSegment(sketch, "E26.1", {"start": v(-8.96, -34.3) * mm, "end": v(-11.51, -35.78) * mm});
            skLineSegment(sketch, "E26.2", {"start": v(-11.51, -35.78) * mm, "end": v(-14.06, -34.3) * mm});
            skLineSegment(sketch, "E26.3", {"start": v(-14.06, -34.3) * mm, "end": v(-14.06, -31.36) * mm});
            skLineSegment(sketch, "E26.4", {"start": v(-14.06, -31.36) * mm, "end": v(-11.51, -29.9) * mm});
            skLineSegment(sketch, "E26.5", {"start": v(-11.51, -29.9) * mm, "end": v(-8.96, -31.36) * mm});
            skPoint(sketch, "E26.0.midPoint", {"position": v(-8.96, -32.84) * mm});
            skLineSegment(sketch, "E27.1.0.0", {"start": v(-5.75, -29.82) * mm, "end": v(-3.2, -31.3) * mm});
            skLineSegment(sketch, "E27.1.0.1", {"start": v(-8.3, -31.3) * mm, "end": v(-5.75, -29.82) * mm});
            skLineSegment(sketch, "E27.1.0.2", {"start": v(-8.3, -34.24) * mm, "end": v(-8.3, -31.3) * mm});
            skLineSegment(sketch, "E27.1.0.3", {"start": v(-5.75, -35.71) * mm, "end": v(-8.3, -34.24) * mm});
            skLineSegment(sketch, "E27.1.0.4", {"start": v(-3.2, -31.3) * mm, "end": v(-3.2, -34.24) * mm});
            skLineSegment(sketch, "E27.1.0.5", {"start": v(-3.2, -34.24) * mm, "end": v(-5.75, -35.71) * mm});
            skLineSegment(sketch, "E27.2.0.0", {"start": v(0.02, -29.75) * mm, "end": v(2.57, -31.23) * mm});
            skLineSegment(sketch, "E27.2.0.1", {"start": v(-2.53, -31.23) * mm, "end": v(0.02, -29.75) * mm});
            skLineSegment(sketch, "E27.2.0.2", {"start": v(-2.53, -34.17) * mm, "end": v(-2.53, -31.23) * mm});
            skLineSegment(sketch, "E27.2.0.3", {"start": v(0.02, -35.64) * mm, "end": v(-2.53, -34.17) * mm});
            skLineSegment(sketch, "E27.2.0.4", {"start": v(2.57, -31.23) * mm, "end": v(2.57, -34.17) * mm});
            skLineSegment(sketch, "E27.2.0.5", {"start": v(2.57, -34.17) * mm, "end": v(0.02, -35.64) * mm});
            skLineSegment(sketch, "E27.3.0.0", {"start": v(5.79, -29.69) * mm, "end": v(8.34, -31.16) * mm});
            skLineSegment(sketch, "E27.3.0.1", {"start": v(3.24, -31.16) * mm, "end": v(5.79, -29.69) * mm});
            skLineSegment(sketch, "E27.3.0.2", {"start": v(3.24, -34.1) * mm, "end": v(3.24, -31.16) * mm});
            skLineSegment(sketch, "E27.3.0.3", {"start": v(5.79, -35.57) * mm, "end": v(3.24, -34.1) * mm});
            skLineSegment(sketch, "E27.3.0.4", {"start": v(8.34, -31.16) * mm, "end": v(8.34, -34.1) * mm});
            skLineSegment(sketch, "E27.3.0.5", {"start": v(8.34, -34.1) * mm, "end": v(5.79, -35.57) * mm});
            skLineSegment(sketch, "E27.direction1", {"start": v(-11.51, -29.9) * mm, "end": v(-5.75, -29.82) * mm, "construction": true});
            skLineSegment(sketch, "E28.0.4.0", {"start": v(11.55, -29.62) * mm, "end": v(14.1, -31.09) * mm});
            skLineSegment(sketch, "E28.3.4.0", {"start": v(9, -31.09) * mm, "end": v(11.55, -29.62) * mm});
            skLineSegment(sketch, "E28.6.4.0", {"start": v(9, -34.03) * mm, "end": v(9, -31.09) * mm});
            skLineSegment(sketch, "E28.9.4.0", {"start": v(11.55, -35.5) * mm, "end": v(9, -34.03) * mm});
            skLineSegment(sketch, "E28.12.4.0", {"start": v(14.1, -31.09) * mm, "end": v(14.1, -34.03) * mm});
            skLineSegment(sketch, "E28.15.4.0", {"start": v(14.1, -34.03) * mm, "end": v(11.55, -35.5) * mm});
            skSolve(sketch);
        }
        {
            var Q0;
            {var subQ4=sQuery(id+"F20.wireOp",EDGE,"E25.1.0.3");Q0=makeQuery(id+"F20.imprint","IMPRINT",FACE,{"disambiguationData":[TD([[makeQuery(id+"F20.imprint","IMPRINT",EDGE,{"derivedFrom":subQ4}),-1.0]])]});}
            var Q1;
            {var subQ4=sQuery(id+"F20.wireOp",EDGE,"E25.2.0.3");Q1=makeQuery(id+"F20.imprint","IMPRINT",FACE,{"disambiguationData":[TD([[makeQuery(id+"F20.imprint","IMPRINT",EDGE,{"derivedFrom":subQ4}),-1.0]])]});}
            var Q2;
            {var subQ5=sQuery(id+"F20.wireOp",EDGE,"E25.3.0.0");Q2=makeQuery(id+"F20.imprint","IMPRINT",FACE,{"disambiguationData":[TD([[makeQuery(id+"F20.imprint","IMPRINT",EDGE,{"derivedFrom":subQ5}),-1.0]])]});}
            var Q3;
            {var subQ0=sQuery(id+"F20.wireOp",EDGE,"E24.1");Q3=makeQuery(id+"F20.imprint","IMPRINT",FACE,{"disambiguationData":[TD([[makeQuery(id+"F20.imprint","IMPRINT",EDGE,{"derivedFrom":subQ0}),-1.0]])]});}
            extrude(context, id + "F22", {"entities" : qUnion([Q0, Q1, Q2, Q3]), "operationType" : NewBodyOperationType.REMOVE, "oppositeDirection" : true, "depth" : 152.4 * mm, "offsetDistance" : 25.4 * mm});
        }
        {
            var Q0;
            Q0=makeQuery(id+"F19.imprint","IMPRINT",FACE,{"disambiguationData":[TD([[makeQuery(id+"F19.imprint","IMPRINT",EDGE,{"derivedFrom":sQuery(id+"F19.wireOp",EDGE,"E21.0")}),-1.0]])]});
            var Q1;
            {var subQ11=sQuery(id+"F19.wireOp",EDGE,"E22.1.0.1");Q1=makeQuery(id+"F19.imprint","IMPRINT",FACE,{"disambiguationData":[TD([[makeQuery(id+"F19.imprint","IMPRINT",EDGE,{"derivedFrom":subQ11}),-1.0]])]});}
            var Q2;
            {var subQ10=sQuery(id+"F19.wireOp",EDGE,"E22.4.0.0");Q2=makeQuery(id+"F19.imprint","IMPRINT",FACE,{"disambiguationData":[TD([[makeQuery(id+"F19.imprint","IMPRINT",EDGE,{"derivedFrom":subQ10}),-1.0]])]});}
            var Q3;
            {var subQ1=sQuery(id+"F19.wireOp",EDGE,"E23.0.5.0");Q3=makeQuery(id+"F19.imprint","IMPRINT",FACE,{"disambiguationData":[TD([[makeQuery(id+"F19.imprint","IMPRINT",EDGE,{"derivedFrom":subQ1}),-1.0]])]});}
            var Q4;
            {var subQ11=sQuery(id+"F21.wireOp",EDGE,"E28.0.4.0");Q4=makeQuery(id+"F21.imprint","IMPRINT",FACE,{"disambiguationData":[TD([[makeQuery(id+"F21.imprint","IMPRINT",EDGE,{"derivedFrom":subQ11}),-1.0]])]});}
            var Q5;
            {var subQ2=sQuery(id+"F21.wireOp",EDGE,"E26.0");Q5=makeQuery(id+"F21.imprint","IMPRINT",FACE,{"disambiguationData":[TD([[makeQuery(id+"F21.imprint","IMPRINT",EDGE,{"derivedFrom":subQ2}),-1.0]])]});}
            extrude(context, id + "F23", {"entities" : qUnion([Q0, Q1, Q2, Q3, Q4, Q5]), "operationType" : NewBodyOperationType.REMOVE, "oppositeDirection" : true, "depth" : 152.4 * mm, "offsetDistance" : 25.4 * mm});
        }
        {
            var Q0;
            Q0=makeQuery(id+"F10.boolean.opBoolean","MERGE",FACE,{"derivedFrom":[makeQuery(id+"F8.opExtrude","CAP_FACE",FACE,{"disambiguationData":[OSD([sQuery(id+"F7.wireOp",EDGE,"E4.0"),sQuery(id+"F7.wireOp",EDGE,"E5.0"),sQuery(id+"F7.wireOp",EDGE,"E7"),sQuery(id+"F7.wireOp",EDGE,"E8")])],"isStart":true}),makeQuery(id+"F10.opExtrude","CAP_FACE",FACE,{"disambiguationData":[OSD([sQuery(id+"F9.wireOp",EDGE,"E9")])],"isStart":false})]});
            var sketch = newSketch(context, id + "F24", { "sketchPlane" : qUnion([Q0])});
            skCircle(sketch, "E29", {"center": v(0, -19.85) * mm, "radius": 17.78 * mm});
            skCircle(sketch, "E30.0", {"center": v(0, -19.85) * mm, "radius": 15.78 * mm});
            skSolve(sketch);
        }
        {
            var Q0;
            Q0 = qSketchRegion(id + "F24", true);
            extrude(context, id + "F25", {"entities" : qUnion([Q0]), "operationType" : NewBodyOperationType.ADD, "oppositeDirection" : true, "depth" : 101.6 * mm, "offsetDistance" : 25.4 * mm});
        }
        {
            var Q0;
            Q0=makeQuery(id+"F25.boolean.opBoolean","SPLIT",FACE,{"derivedFrom":makeQuery(id+"F25.opExtrude","CAP_FACE",FACE,{"disambiguationData":[OSD([sQuery(id+"F24.wireOp",EDGE,"E29"),sQuery(id+"F24.wireOp",EDGE,"E30.0")])],"isStart":true})});
            extrude(context, id + "F26", {"entities" : qUnion([Q0]), "operationType" : NewBodyOperationType.REMOVE, "oppositeDirection" : true, "depth" : 101.6 * mm, "offsetDistance" : 25.4 * mm});
        }
    });
